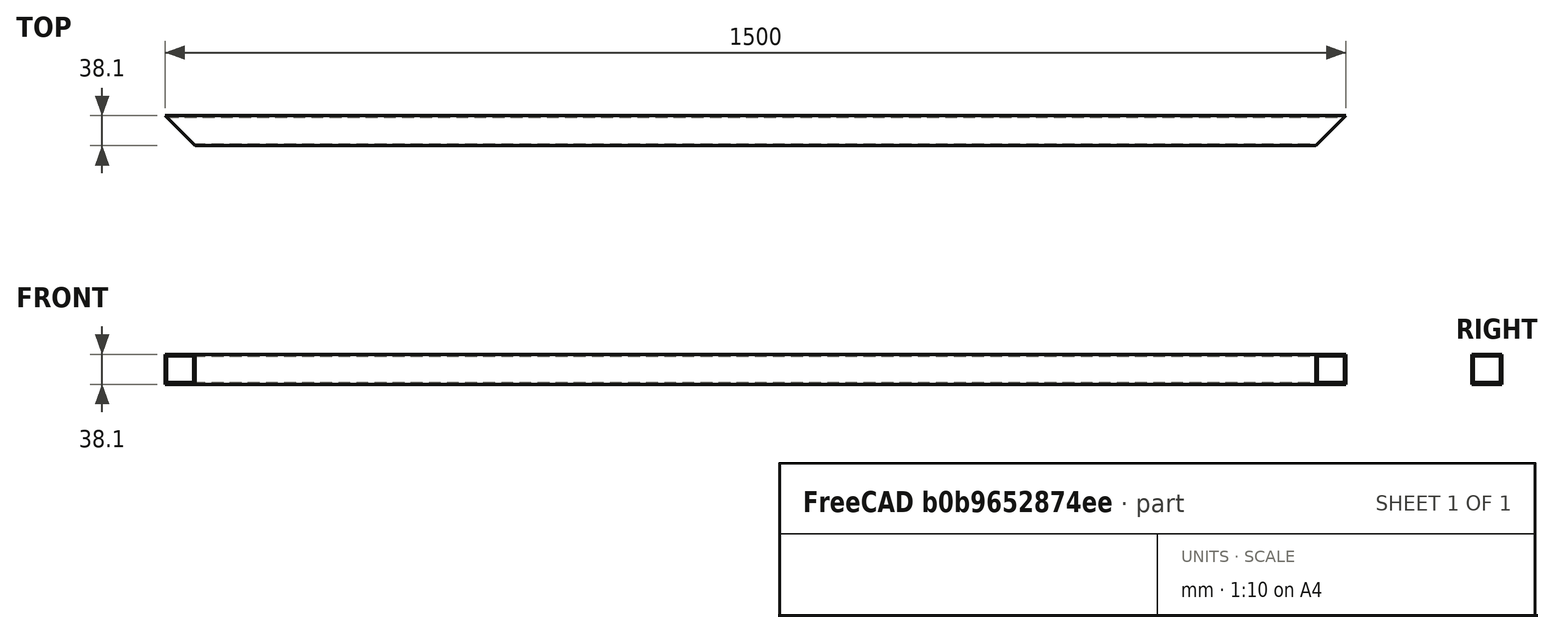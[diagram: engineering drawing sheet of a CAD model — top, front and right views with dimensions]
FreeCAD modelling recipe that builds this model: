
FCSTD DOCUMENT  (FreeCAD 0.18.4R)
Label: sp_ptc1ymedia(cal14)(150cm)(cut45)
License: All rights reserved
LicenseURL: http://en.wikipedia.org/wiki/All_rights_reserved
objects: Part::Cut×3, Part::Box×2, Part::Extrusion×2, App::MeasureDistance×1
note: 7 computed .brp shape members not serialized (recipe doc carries the construction recipe); baked Part::Feature solids carry a one-line shape summary decoded from their .brp

FEATURE [Part::Box] Box  label="Cuboexterno"
  AttacherType = Attacher::AttachEngine3D
  Height = 38.1
  Length = 3000
  Width = 38.1
FEATURE [Part::Box] Box001  label="CuboInterno"
  AttacherType = Attacher::AttachEngine3D
  Height = 34.1
  Length = 3000
  Placement = pos=(0,2,2) rot=(0,0,1;0rad)
  Width = 34.1
FEATURE [Part::Cut] Cut  label="sp_ptc1ymedia(cal14)(300cm)(cut90)"
  Base = -> Box
  Tool = -> Box001
FEATURE [Part::Extrusion] Extrude  label="cortador45Der"
  Dir = (0,0,1)
  DirMode = 2
  FaceMakerClass = Part::FaceMakerBullseye
  LengthFwd = 100
  LengthRev = 0
  Placement = pos=(1461.9,0,0) rot=(0,0,1;0rad)
  Solid = true
  Symmetric = false
FEATURE [Part::Extrusion] Extrude001  label="cortador45Izq"
  Dir = (0,0,1)
  DirMode = 2
  FaceMakerClass = Part::FaceMakerBullseye
  LengthFwd = 100
  LengthRev = 0
  Placement = pos=(38.1,0,0) rot=(0,0,1;0rad)
  Solid = true
  Symmetric = false
FEATURE [Part::Cut] Cut001
  Base = -> Cut
  Tool = -> Extrude
FEATURE [Part::Cut] Cut002  label="sp_ptc1ymedia(cal14)(150cm)(cut45)"
  Base = -> Cut001
  Tool = -> Extrude001
FEATURE [App::MeasureDistance] Distance  label="Distance: 1500.00 mm"
  Distance = 1500
  P1 = (0,38.1,38.1)
  P2 = (1500,38.1,38.1)
